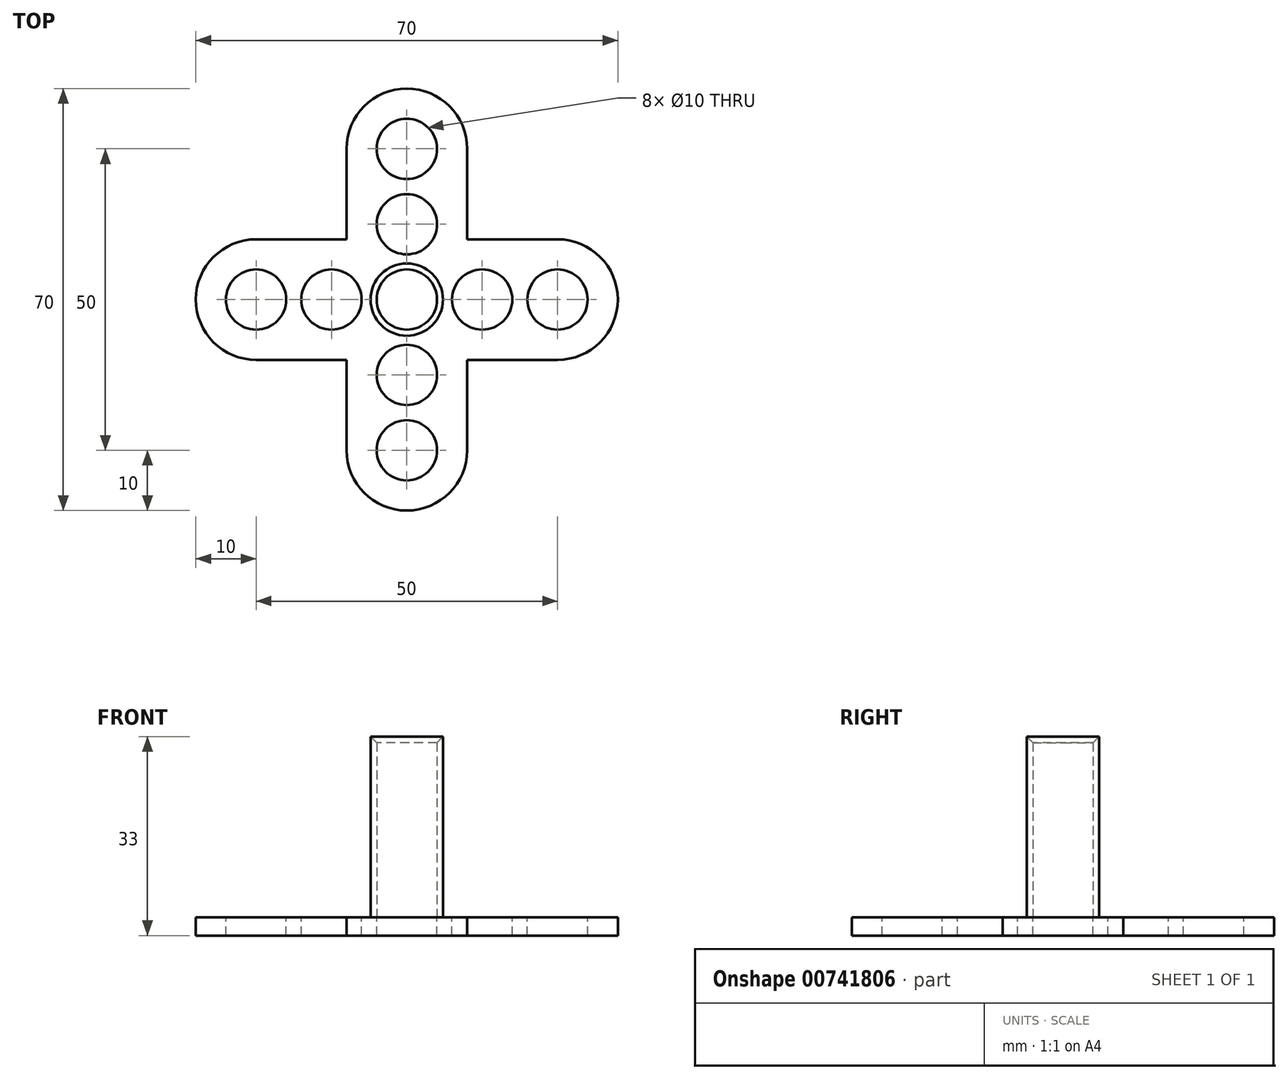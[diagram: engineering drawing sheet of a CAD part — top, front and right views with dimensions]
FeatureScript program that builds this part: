
annotation { "Feature Type Name" : "Feature", "Feature Type Description" : "" }
export const myFeature = defineFeature(function(context is Context, id is Id, definition is map)
    precondition{}
    {
        {
            var Q0;
            Q0=qCreatedBy(makeId("Top.planeOp"),FACE);
            var sketch = newSketch(context, id + "F0", { "sketchPlane" : qUnion([Q0])});
            skLineSegment(sketch, "E0.bottom", {"start": v(0, 35) * mm, "end": v(0, 35) * mm});
            skLineSegment(sketch, "E0.top", {"start": v(0, -35) * mm, "end": v(0, -35) * mm});
            skLineSegment(sketch, "E0.left", {"start": v(10, 25) * mm, "end": v(10, 10) * mm});
            skLineSegment(sketch, "E0.right", {"start": v(-10, 25) * mm, "end": v(-10, 10) * mm});
            skPoint(sketch, "E0.middle", {"position": v(0, 0) * mm});
            skLineSegment(sketch, "E1.bottom", {"start": v(25, 10) * mm, "end": v(10, 10) * mm});
            skLineSegment(sketch, "E1.top", {"start": v(25, -10) * mm, "end": v(10, -10) * mm});
            skLineSegment(sketch, "E1.left", {"start": v(35, 0) * mm, "end": v(35, 0) * mm});
            skLineSegment(sketch, "E1.right", {"start": v(-35, 0) * mm, "end": v(-35, 0) * mm});
            skLineSegment(sketch, "E2.trimOffspring", {"start": v(-10, 10) * mm, "end": v(-25, 10) * mm});
            skLineSegment(sketch, "E3.trimOffspring", {"start": v(-10, -10) * mm, "end": v(-10, -25) * mm});
            skLineSegment(sketch, "E4.trimOffspring", {"start": v(-10, -10) * mm, "end": v(-25, -10) * mm});
            skLineSegment(sketch, "E5.trimOffspring", {"start": v(10, -10) * mm, "end": v(10, -25) * mm});
            skPoint(sketch, "E6.visualSharp", {"position": v(-35, 10) * mm});
            skArc(sketch, "E6.filletArc", {"start": v(-25, 10) * mm, "mid": v(-32.07, 7.07) * mm, "end": v(-35, 0) * mm});
            skPoint(sketch, "E7.visualSharp", {"position": v(-35, -10) * mm});
            skArc(sketch, "E7.filletArc", {"start": v(-35, 0) * mm, "mid": v(-32.07, -7.07) * mm, "end": v(-25, -10) * mm});
            skPoint(sketch, "E8.visualSharp", {"position": v(-10, -35) * mm});
            skArc(sketch, "E8.filletArc", {"start": v(-10, -25) * mm, "mid": v(-7.07, -32.07) * mm, "end": v(0, -35) * mm});
            skPoint(sketch, "E9.visualSharp", {"position": v(10, -35) * mm});
            skArc(sketch, "E9.filletArc", {"start": v(0, -35) * mm, "mid": v(7.07, -32.07) * mm, "end": v(10, -25) * mm});
            skPoint(sketch, "E10.visualSharp", {"position": v(35, -10) * mm});
            skArc(sketch, "E10.filletArc", {"start": v(25, -10) * mm, "mid": v(32.07, -7.07) * mm, "end": v(35, 0) * mm});
            skPoint(sketch, "E11.visualSharp", {"position": v(35, 10) * mm});
            skArc(sketch, "E11.filletArc", {"start": v(35, 0) * mm, "mid": v(32.07, 7.07) * mm, "end": v(25, 10) * mm});
            skPoint(sketch, "E12.visualSharp", {"position": v(10, 35) * mm});
            skArc(sketch, "E12.filletArc", {"start": v(10, 25) * mm, "mid": v(7.07, 32.07) * mm, "end": v(0, 35) * mm});
            skPoint(sketch, "E13.visualSharp", {"position": v(-10, 35) * mm});
            skArc(sketch, "E13.filletArc", {"start": v(0, 35) * mm, "mid": v(-7.07, 32.07) * mm, "end": v(-10, 25) * mm});
            skSolve(sketch);
        }
        {
            var Q0;
            Q0 = qSketchRegion(id + "F0", true);
            extrude(context, id + "F1", {"entities" : qUnion([Q0]), "depth" : 3 * mm, "offsetDistance" : 25 * mm});
        }
        {
            var Q0;
            Q0=makeQuery(id+"F1.opExtrude","CAP_FACE",FACE,{"disambiguationData":[OSD([sQuery(id+"F0.wireOp",EDGE,"E0.left"),sQuery(id+"F0.wireOp",EDGE,"E0.right"),sQuery(id+"F0.wireOp",EDGE,"E1.bottom"),sQuery(id+"F0.wireOp",EDGE,"E1.top"),sQuery(id+"F0.wireOp",EDGE,"E2.trimOffspring"),sQuery(id+"F0.wireOp",EDGE,"E3.trimOffspring"),sQuery(id+"F0.wireOp",EDGE,"E4.trimOffspring"),sQuery(id+"F0.wireOp",EDGE,"E5.trimOffspring"),sQuery(id+"F0.wireOp",EDGE,"E6.filletArc"),sQuery(id+"F0.wireOp",EDGE,"E7.filletArc"),sQuery(id+"F0.wireOp",EDGE,"E8.filletArc"),sQuery(id+"F0.wireOp",EDGE,"E9.filletArc"),sQuery(id+"F0.wireOp",EDGE,"E10.filletArc"),sQuery(id+"F0.wireOp",EDGE,"E11.filletArc"),sQuery(id+"F0.wireOp",EDGE,"E12.filletArc"),sQuery(id+"F0.wireOp",EDGE,"E13.filletArc")])],"isStart":false});
            var sketch = newSketch(context, id + "F2", { "sketchPlane" : qUnion([Q0])});
            skLineSegment(sketch, "E14", {"start": v(0, 35) * mm, "end": v(0, -35) * mm, "construction": true});
            skLineSegment(sketch, "E15", {"start": v(35, 0) * mm, "end": v(-35, 0) * mm, "construction": true});
            skPoint(sketch, "E16", {"position": v(0, 25) * mm});
            skPoint(sketch, "E17", {"position": v(25, 0) * mm});
            skPoint(sketch, "E18", {"position": v(-25, 0) * mm});
            skPoint(sketch, "E19", {"position": v(0, -25) * mm});
            skLineSegment(sketch, "E20", {"start": v(0, 0) * mm, "end": v(0, -25) * mm});
            skLineSegment(sketch, "E21", {"start": v(25, 0) * mm, "end": v(0, 0) * mm});
            skLineSegment(sketch, "E22", {"start": v(0, 25) * mm, "end": v(0, 0) * mm});
            skLineSegment(sketch, "E23", {"start": v(-25, 0) * mm, "end": v(0, 0) * mm});
            skPoint(sketch, "E24", {"position": v(-12.5, 0) * mm});
            skPoint(sketch, "E25", {"position": v(0, 12.5) * mm});
            skPoint(sketch, "E26", {"position": v(12.5, 0) * mm});
            skPoint(sketch, "E27", {"position": v(0, -12.5) * mm});
            skSolve(sketch);
        }
        {
            var Q0;
            Q0=sQuery(id+"F2.wireOp",VERTEX,"E18");
            var Q1;
            Q1=sQuery(id+"F2.wireOp",VERTEX,"E24");
            var Q2;
            Q2=sQuery(id+"F2.wireOp",VERTEX,"E16");
            var Q3;
            Q3=sQuery(id+"F2.wireOp",VERTEX,"E25");
            var Q4;
            Q4=sQuery(id+"F2.wireOp",VERTEX,"E26");
            var Q5;
            Q5=sQuery(id+"F2.wireOp",VERTEX,"E17");
            var Q6;
            Q6=sQuery(id+"F2.wireOp",VERTEX,"E27");
            var Q7;
            Q7=sQuery(id+"F2.wireOp",VERTEX,"E19");
            var Q8;
            Q8=makeQuery(id+"F1.opExtrude","SWEPT_BODY",BODY,{"disambiguationData":[OSD([sQuery(id+"F0.wireOp",EDGE,"E0.left"),sQuery(id+"F0.wireOp",EDGE,"E0.right"),sQuery(id+"F0.wireOp",EDGE,"E1.bottom"),sQuery(id+"F0.wireOp",EDGE,"E1.top"),sQuery(id+"F0.wireOp",EDGE,"E2.trimOffspring"),sQuery(id+"F0.wireOp",EDGE,"E3.trimOffspring"),sQuery(id+"F0.wireOp",EDGE,"E4.trimOffspring"),sQuery(id+"F0.wireOp",EDGE,"E5.trimOffspring"),sQuery(id+"F0.wireOp",EDGE,"E6.filletArc"),sQuery(id+"F0.wireOp",EDGE,"E7.filletArc"),sQuery(id+"F0.wireOp",EDGE,"E8.filletArc"),sQuery(id+"F0.wireOp",EDGE,"E9.filletArc"),sQuery(id+"F0.wireOp",EDGE,"E10.filletArc"),sQuery(id+"F0.wireOp",EDGE,"E11.filletArc"),sQuery(id+"F0.wireOp",EDGE,"E12.filletArc"),sQuery(id+"F0.wireOp",EDGE,"E13.filletArc")])]});
            hole(context, id + "F3", {"style" : HoleStyle.SIMPLE, "endStyle" : HoleEndStyle.THROUGH, "holeDiameter" : 10 * mm, "majorDiameter" : 5 * mm, "isTappedThrough" : true, "tappedDepth" : 12 * mm, "tapClearance" : 3, "locations" : qUnion([Q0, Q1, Q2, Q3, Q4, Q5, Q6, Q7]), "scope" : qUnion([Q8])});
        }
        {
            var Q0;
            Q0=makeQuery(id+"F1.opExtrude","CAP_FACE",FACE,{"disambiguationData":[OSD([sQuery(id+"F0.wireOp",EDGE,"E0.left"),sQuery(id+"F0.wireOp",EDGE,"E0.right"),sQuery(id+"F0.wireOp",EDGE,"E1.bottom"),sQuery(id+"F0.wireOp",EDGE,"E1.top"),sQuery(id+"F0.wireOp",EDGE,"E2.trimOffspring"),sQuery(id+"F0.wireOp",EDGE,"E3.trimOffspring"),sQuery(id+"F0.wireOp",EDGE,"E4.trimOffspring"),sQuery(id+"F0.wireOp",EDGE,"E5.trimOffspring"),sQuery(id+"F0.wireOp",EDGE,"E6.filletArc"),sQuery(id+"F0.wireOp",EDGE,"E7.filletArc"),sQuery(id+"F0.wireOp",EDGE,"E8.filletArc"),sQuery(id+"F0.wireOp",EDGE,"E9.filletArc"),sQuery(id+"F0.wireOp",EDGE,"E10.filletArc"),sQuery(id+"F0.wireOp",EDGE,"E11.filletArc"),sQuery(id+"F0.wireOp",EDGE,"E12.filletArc"),sQuery(id+"F0.wireOp",EDGE,"E13.filletArc")])],"isStart":false});
            var sketch = newSketch(context, id + "F4", { "sketchPlane" : qUnion([Q0])});
            skCircle(sketch, "E28", {"center": v(0, 0) * mm, "radius": 6 * mm});
            skCircle(sketch, "E29", {"center": v(0, 0) * mm, "radius": 5 * mm});
            skSolve(sketch);
        }
        {
            var Q0;
            Q0 = qSketchRegion(id + "F4", true);
            extrude(context, id + "F5", {"entities" : qUnion([Q0]), "operationType" : NewBodyOperationType.ADD, "depth" : 30 * mm, "offsetDistance" : 25 * mm});
        }
        {
            var Q0;
            Q0=makeQuery(id+"F5.opExtrude","CAP_EDGE",EDGE,{"disambiguationData":[OSD([sQuery(id+"F4.wireOp",EDGE,"E29")])],"isStart":false});
            chamfer(context, id + "F6", {"entities" : qUnion([Q0]), "width" : 1 * mm, "tangentPropagation" : true});
        }
    });
